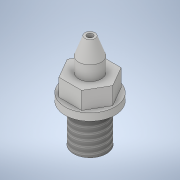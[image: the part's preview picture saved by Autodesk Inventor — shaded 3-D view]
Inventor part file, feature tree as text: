
AUTODESK INVENTOR PART (.ipt)
format: ipt  version: 2021 (Build 250183000, 183)  size: 148,480 bytes
history: native  units: mm
features: sketch x6, extrude x5, plane x1, loft x1, thread x1, other x1
ambient origin geometry x8: Origin, YZ Plane, XZ Plane, XY Plane, X Axis, Y Axis, Z Axis, Center Point
bodies: Solid1 (feature_tree)
feature tree (15):
  extrude  "Extrusion1"  Depth=5.0mm TaperAngle=0.0deg
  plane  "Work Plane1"
  loft  "Loft1"
  sketch  "Sketch3"  dims[d5=0.0mm d6=90.0deg d7=0.0mm d8=90.0deg]
  extrude  "Extrusion2"  TaperAngle=0.0deg  [1 undecoded]
  extrude  "Extrusion3"  Depth=6.0mm TaperAngle=0.0deg
  extrude  "Extrusion4"  Depth=2.5mm TaperAngle=0.0deg
  thread  "Thread1"  [1 undecoded]
  extrude  "Extrusion5"  Depth=13.6mm TaperAngle=0.0deg
  sketch  "Sketch1"  dims[d0=7.8mm d1=5.0mm d2=0.0mm]
  sketch  "Sketch2"  dims[d3=6.0mm d4=3.5mm]
  other  "Edges1"
  sketch  "Sketch4"  dims[d9=2.0mm d10=6.0mm d11=0.0mm]
  sketch  "Sketch5"  dims[d12=17.2mm d13=2.5mm d14=0.0mm d15=11.3mm]
  sketch  "Sketch6"  dims[d16=13.0mm d17=0.0mm d18=14.0mm d19=0.0mm d20=14.0mm d21=0.0mm d22=13.6mm]
note: 2 required parameter values undecoded (feature->parameter linkage not recoverable at this tier; creation-order binding heuristic only, values carry confidence <= 0.55)
